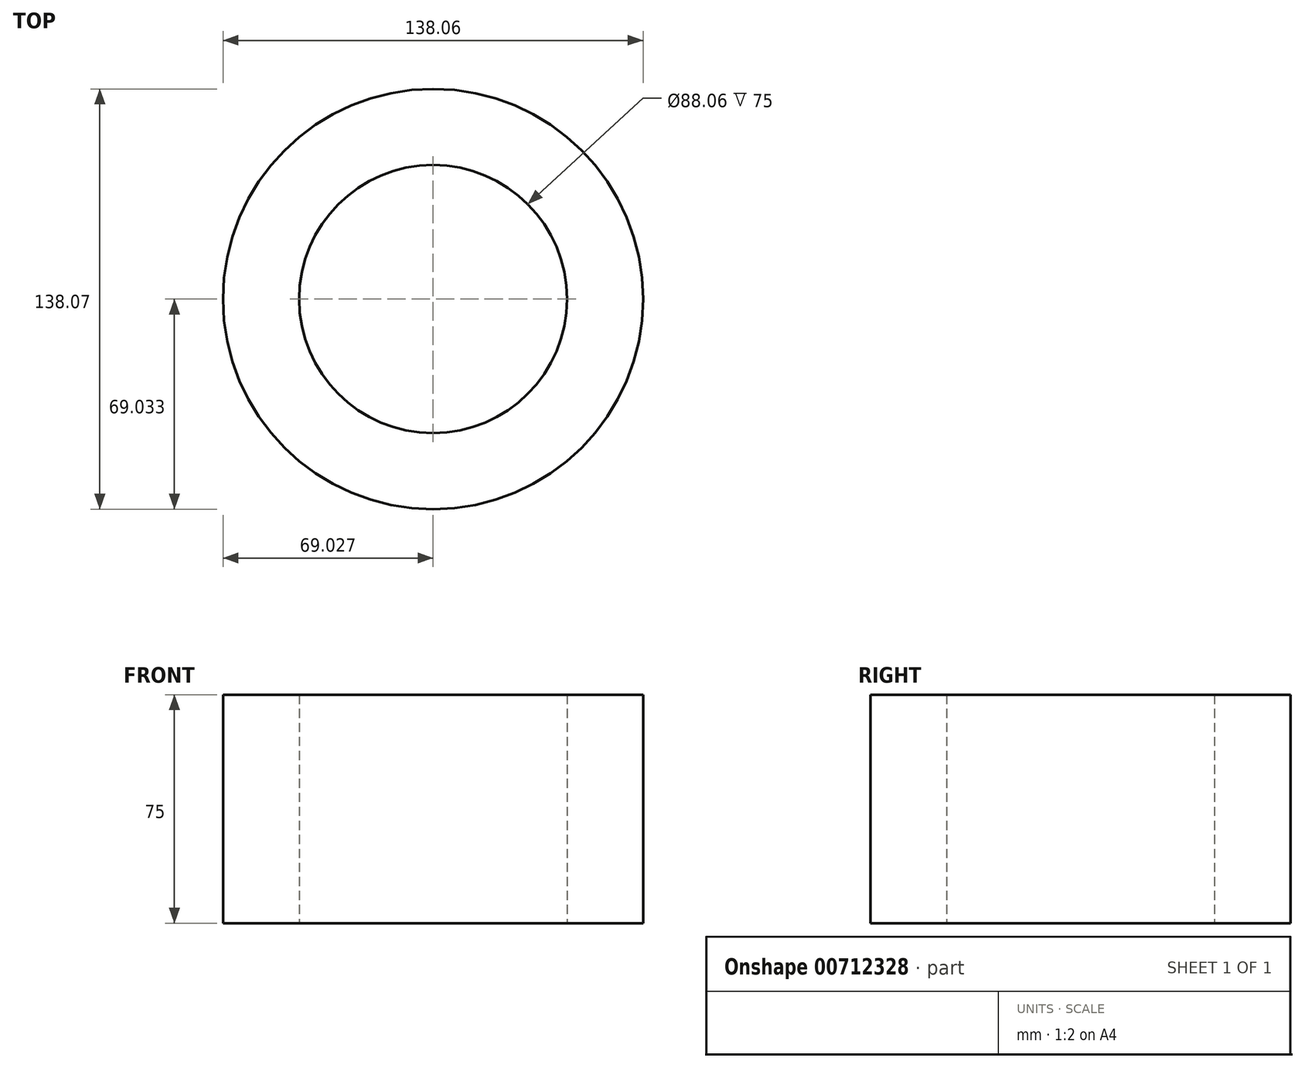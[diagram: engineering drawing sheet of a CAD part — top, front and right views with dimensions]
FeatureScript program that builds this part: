
annotation { "Feature Type Name" : "Feature", "Feature Type Description" : "" }
export const myFeature = defineFeature(function(context is Context, id is Id, definition is map)
    precondition{}
    {
        {
            var Q0;
            Q0=qCreatedBy(makeId("Top.planeOp"),FACE);
            var sketch = newSketch(context, id + "F0", { "sketchPlane" : qUnion([Q0])});
            skCircle(sketch, "E0", {"center": v(-16.77, 9.4) * mm, "radius": 44.03 * mm});
            skCircle(sketch, "E1.0", {"center": v(-16.77, 9.4) * mm, "radius": 69.03 * mm});
            skLineSegment(sketch, "E2.bottom", {"start": v(-108.93, 85.68) * mm, "end": v(81.3, 85.68) * mm});
            skLineSegment(sketch, "E2.top", {"start": v(-108.93, -79.5) * mm, "end": v(81.3, -79.5) * mm});
            skLineSegment(sketch, "E2.left", {"start": v(-108.93, 85.68) * mm, "end": v(-108.93, -79.5) * mm});
            skLineSegment(sketch, "E2.right", {"start": v(81.3, 85.68) * mm, "end": v(81.3, -79.5) * mm});
            skLineSegment(sketch, "E3.0", {"start": v(111.3, 85.68) * mm, "end": v(111.3, -79.5) * mm});
            skCircle(sketch, "E4.0", {"center": v(-16.77, 9.4) * mm, "radius": 98.65 * mm});
            skSolve(sketch);
        }
        {
            var Q0;
            Q0=makeQuery(id+"F0.imprint","IMPRINT",FACE,{"disambiguationData":[TD([[makeQuery(id+"F0.imprint","IMPRINT",EDGE,{"derivedFrom":sQuery(id+"F0.wireOp",EDGE,"E0")}),-1.0]])]});
            extrude(context, id + "F1", {"entities" : qUnion([Q0]), "depth" : 75 * mm, "offsetDistance" : 25 * mm});
        }
    });
